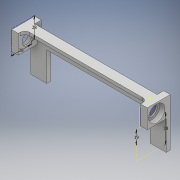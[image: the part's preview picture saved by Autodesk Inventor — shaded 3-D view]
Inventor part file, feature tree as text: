
AUTODESK INVENTOR PART (.ipt)
format: ipt  version: 2018 (Build 220112000, 112)  size: 242,688 bytes
history: native  units: mm
features: sketch x15, extrude x10, plane x1, fillet x1
ambient origin geometry x8: Origin, YZ Plane, XZ Plane, XY Plane, X Axis, Y Axis, Z Axis, Center Point
bodies: Solid1 (feature_tree)
feature tree (27):
  extrude  "Extrusion1"  Depth=22.5mm
  extrude  "Extrusion2"  Depth=26.0mm
  extrude  "Extrusion3"  Depth=9.0mm TaperAngle=0.0deg
  extrude  "Extrusion4"  Depth=2.0mm TaperAngle=0.0deg
  extrude  "Extrusion5"  Depth=26.0mm
  extrude  "Extrusion6"  Depth=9.0mm TaperAngle=0.0deg
  plane  "Work Plane1"
  extrude  "Extrusion7"  Depth=5.5mm TaperAngle=0.0deg
  sketch  "Sketch8"  dims[d20=0.0mm d21=9.25mm d22=9.0mm]
  sketch  "Sketch9"  dims[d23=168.0mm d24=0.0mm d25=9.0mm]
  extrude  "Extrusion8"  Depth=9.25mm
  fillet  "Fillet1"  Radius=9.0mm
  sketch  "Sketch11"  dims[d29=22.0mm]
  extrude  "Extrusion9"  Depth=9.0mm
  extrude  "Extrusion10"  Depth=6.5mm
  sketch  "Sketch14"  dims[d32=22.0mm]
  sketch  "Sketch15"  dims[d33=12.2mm d34=3.2mm d35=40.0mm d36=0.0mm d37=15.0mm d38=0.0mm d39=28.0mm d40=28.0mm d41=19.0mm d45=38.0mm]
  sketch  "Sketch1"  dims[d0=22.5mm d1=3.0mm]
  sketch  "Sketch2"  dims[d2=3.0mm d3=26.0mm]
  sketch  "Sketch3"  dims[d4=26.0mm d5=9.0mm d6=0.0mm]
  sketch  "Sketch4"  dims[d7=15.5mm d8=2.0mm d9=0.0mm]
  sketch  "Sketch5"  dims[d10=4.25mm d11=26.0mm]
  sketch  "Sketch6"  dims[d12=168.0mm d13=0.0mm d14=9.0mm d15=0.0mm]
  sketch  "Sketch7"  dims[d16=2.0mm d17=0.0mm d18=5.5mm d19=0.0mm]
  sketch  "Sketch10"  dims[d26=5.0mm d27=0.0mm d28=6.5mm]
  sketch  "Sketch12"  dims[d30=12.2mm]
  sketch  "Sketch13"  dims[d31=3.2mm]
